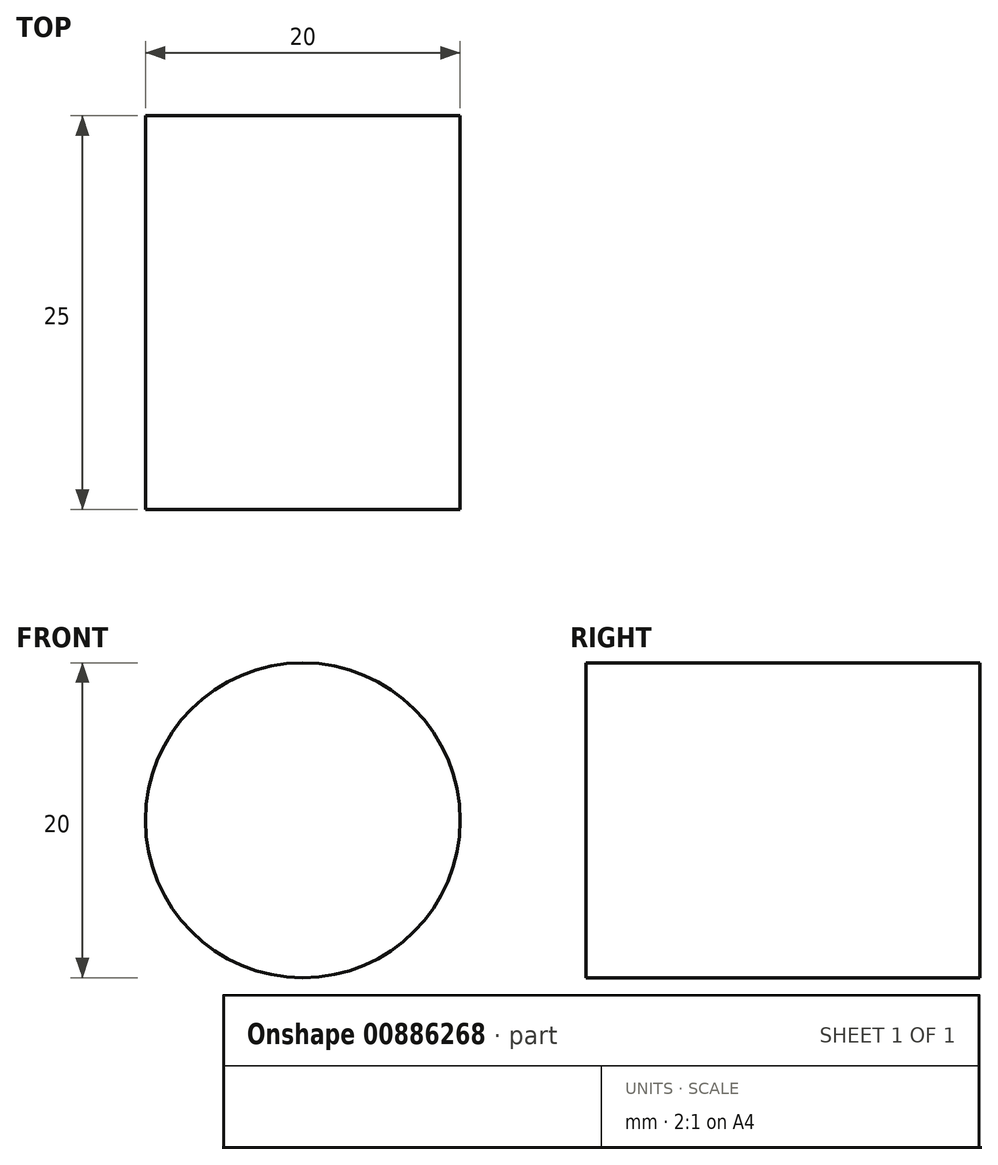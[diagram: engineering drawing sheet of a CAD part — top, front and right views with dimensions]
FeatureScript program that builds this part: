
annotation { "Feature Type Name" : "Feature", "Feature Type Description" : "" }
export const myFeature = defineFeature(function(context is Context, id is Id, definition is map)
    precondition{}
    {
        {
            var Q0;
            Q0=qCreatedBy(makeId("Front.planeOp"),FACE);
            var sketch = newSketch(context, id + "F0", { "sketchPlane" : qUnion([Q0])});
            skCircle(sketch, "E0", {"center": v(0, 0) * mm, "radius": 10 * mm});
            skSolve(sketch);
        }
        {
            var Q0;
            Q0 = qSketchRegion(id + "F0", true);
            extrude(context, id + "F1", {"entities" : qUnion([Q0]), "depth" : 25 * mm, "offsetDistance" : 25 * mm, "symmetric" : true});
        }
    });
